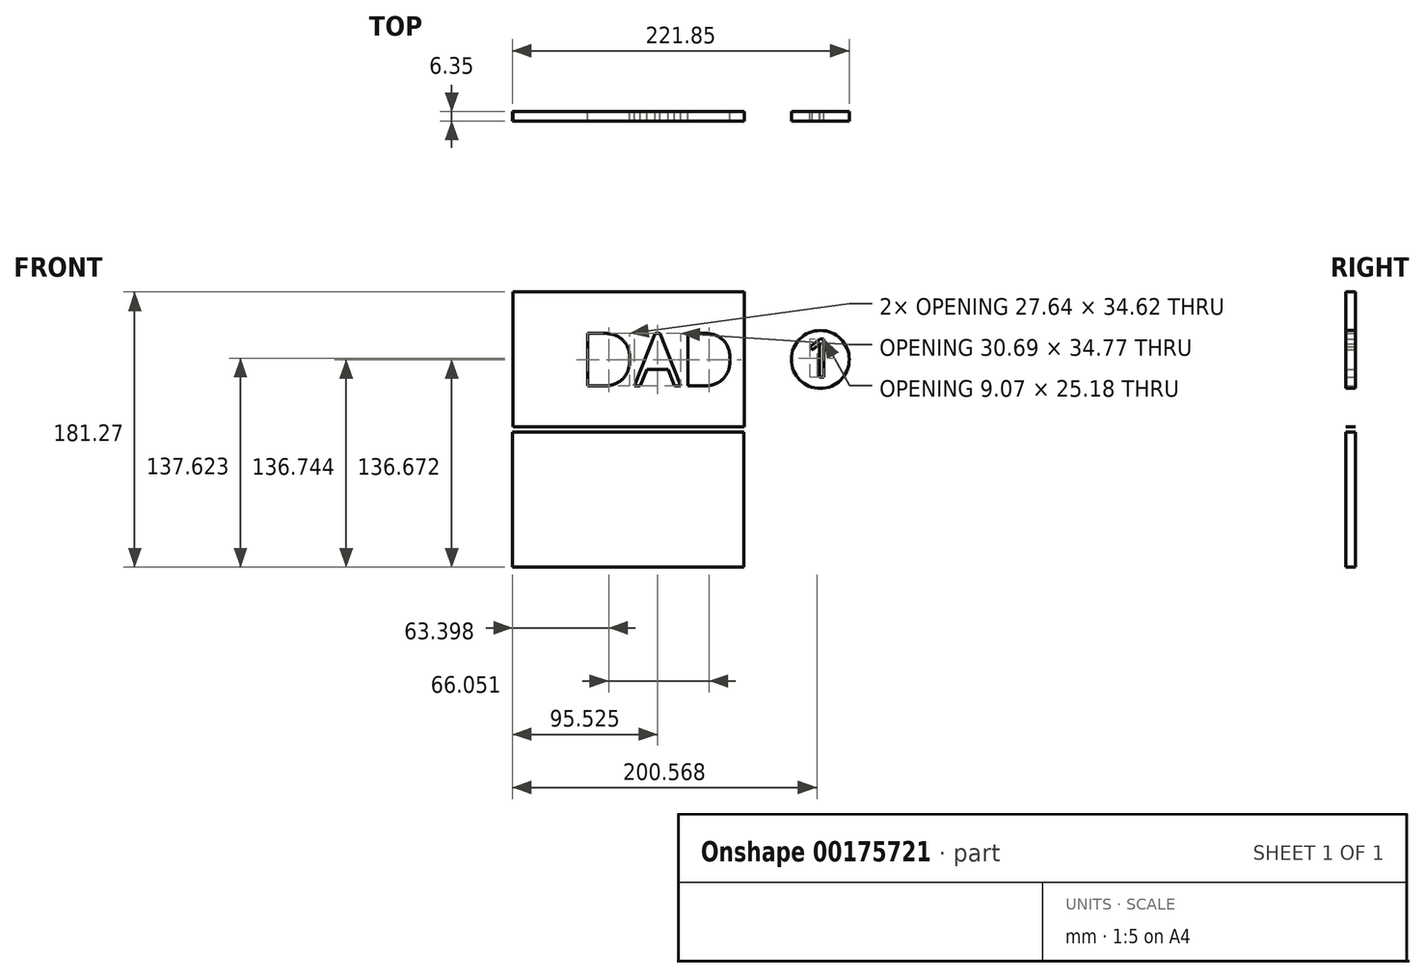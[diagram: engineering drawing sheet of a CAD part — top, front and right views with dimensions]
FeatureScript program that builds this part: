
annotation { "Feature Type Name" : "Feature", "Feature Type Description" : "" }
export const myFeature = defineFeature(function(context is Context, id is Id, definition is map)
    precondition{}
    {
        {
            var Q0;
            Q0=qCreatedBy(makeId("Front.planeOp"),FACE);
            var sketch = newSketch(context, id + "F0", { "sketchPlane" : qUnion([Q0])});
            skLineSegment(sketch, "E0.bottom", {"start": v(-7.02, 64.2) * mm, "end": v(50.13, 64.2) * mm});
            skLineSegment(sketch, "E0.top", {"start": v(-102.27, -24.7) * mm, "end": v(50.13, -24.7) * mm});
            skLineSegment(sketch, "E0.left", {"start": v(-102.27, 64.2) * mm, "end": v(-102.27, -24.7) * mm});
            skLineSegment(sketch, "E0.right", {"start": v(50.13, 64.2) * mm, "end": v(50.13, -24.7) * mm});
            skText(sketch, "E1", { "text": "DAD", "fontName": "OpenSans-Regular.ttf"});
            skLineSegment(sketch, "E2", {"start": v(-7.02, 37.2) * mm, "end": v(-7.02, 64.2) * mm});
            skLineSegment(sketch, "E3", {"start": v(-7.02, 2.28) * mm, "end": v(-7.02, -24.7) * mm});
            skLineSegment(sketch, "E4", {"start": v(-102.27, 64.2) * mm, "end": v(-7.02, 64.2) * mm});
            skPoint(sketch, "E5", {"position": v(-26.07, -24.7) * mm});
            skPoint(sketch, "E6", {"position": v(-102.27, 19.74) * mm});
            skLineSegment(sketch, "E7.bottom", {"start": v(-7.39, -28.18) * mm, "end": v(49.76, -28.18) * mm});
            skLineSegment(sketch, "E7.top", {"start": v(-102.64, -117.08) * mm, "end": v(49.76, -117.08) * mm});
            skLineSegment(sketch, "E7.left", {"start": v(-102.64, -28.18) * mm, "end": v(-102.64, -117.08) * mm});
            skLineSegment(sketch, "E7.right", {"start": v(49.76, -28.18) * mm, "end": v(49.76, -117.08) * mm});
            skLineSegment(sketch, "E8", {"start": v(-102.64, -28.18) * mm, "end": v(-7.39, -28.18) * mm});
            skCircle(sketch, "E9", {"center": v(100.16, 19.74) * mm, "radius": 19.05 * mm});
            skText(sketch, "E10", { "text": "1", "fontName": "OpenSans-Regular.ttf"});
            const initialGuessF0  = {"E1": [-0.05782, 0.00228, 1, 0, 0.03492], "E10": [0.09015, 0.00795, 1, 0, 0.0254]};
            skSetInitialGuess(sketch, initialGuessF0);
            skSolve(sketch);
        }
        {
            var Q0;
            Q0=makeQuery(id+"F0.imprint","IMPRINT",FACE,{"disambiguationData":[TD([[makeQuery(id+"F0.imprint","IMPRINT",EDGE,{"derivedFrom":sQuery(id+"F0.wireOp",EDGE,"E9")}),1.0]])]});
            extrude(context, id + "F1", {"entities" : qUnion([Q0]), "depth" : 6.35 * mm});
        }
        {
            var Q0;
            Q0=makeQuery(id+"F0.imprint","IMPRINT",FACE,{"disambiguationData":[TD([[makeQuery(id+"F0.imprint","IMPRINT",EDGE,{"derivedFrom":sQuery(id+"F0.wireOp",EDGE,"E0.bottom")}),-1.0]])]});
            extrude(context, id + "F2", {"entities" : qUnion([Q0]), "depth" : 6.35 * mm});
        }
        {
            var Q0;
            Q0=makeQuery(id+"F0.imprint","IMPRINT",FACE,{"disambiguationData":[TD([[makeQuery(id+"F0.imprint","IMPRINT",EDGE,{"derivedFrom":sQuery(id+"F0.wireOp",EDGE,"E7.bottom")}),-1.0]])]});
            extrude(context, id + "F3", {"entities" : qUnion([Q0]), "depth" : 6.35 * mm});
        }
    });
